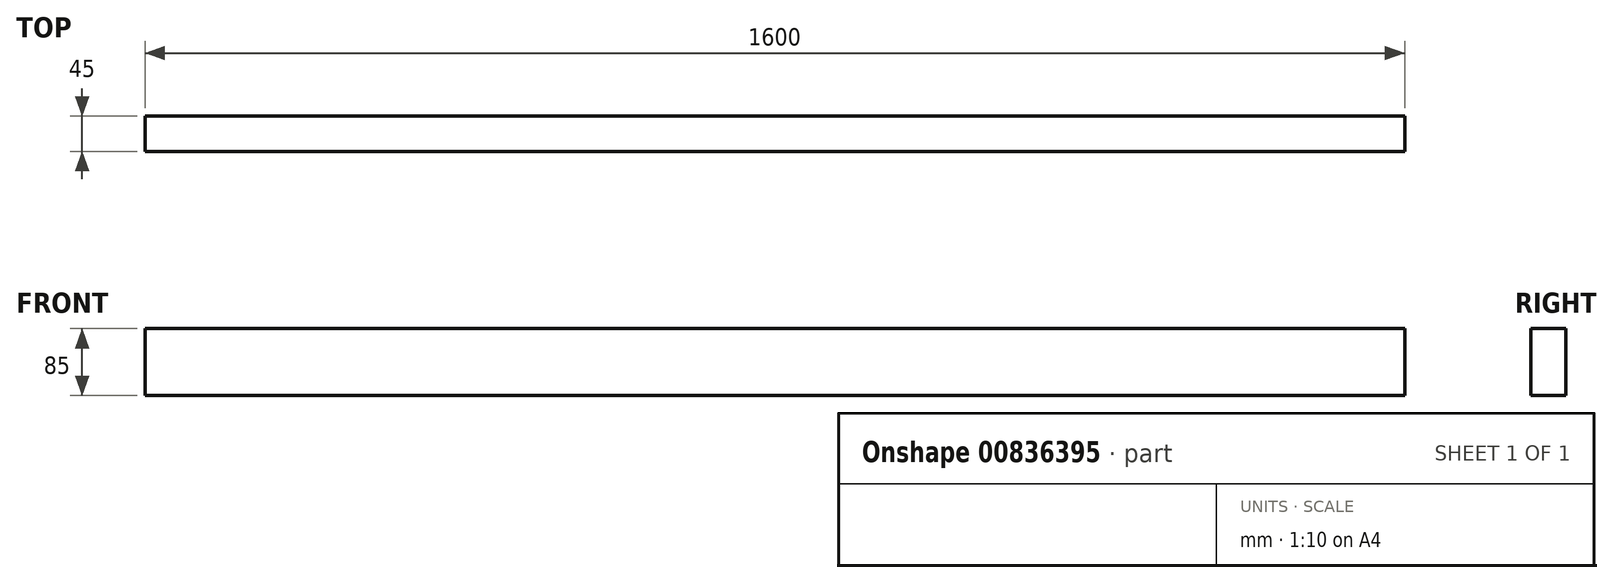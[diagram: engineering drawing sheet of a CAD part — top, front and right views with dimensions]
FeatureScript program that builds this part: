
annotation { "Feature Type Name" : "Feature", "Feature Type Description" : "" }
export const myFeature = defineFeature(function(context is Context, id is Id, definition is map)
    precondition{}
    {
        {
            var Q0;
            Q0=qCreatedBy(makeId("Front.planeOp"),FACE);
            var sketch = newSketch(context, id + "F0", { "sketchPlane" : qUnion([Q0])});
            skLineSegment(sketch, "E0.bottom", {"start": v(-700.53, 0) * mm, "end": v(899.47, 0) * mm});
            skLineSegment(sketch, "E0.top", {"start": v(-700.53, 85) * mm, "end": v(899.47, 85) * mm});
            skLineSegment(sketch, "E0.left", {"start": v(-700.53, 0) * mm, "end": v(-700.53, 85) * mm});
            skLineSegment(sketch, "E0.right", {"start": v(899.47, 0) * mm, "end": v(899.47, 85) * mm});
            skSolve(sketch);
        }
        {
            var Q0;
            Q0=makeQuery(id+"F0.imprint","IMPRINT",FACE,{"disambiguationData":[TD([[makeQuery(id+"F0.imprint","IMPRINT",EDGE,{"derivedFrom":sQuery(id+"F0.wireOp",EDGE,"E0.bottom")}),1.0]])]});
            extrude(context, id + "F1", {"entities" : qUnion([Q0]), "depth" : 45 * mm, "offsetDistance" : 25 * mm});
        }
    });
